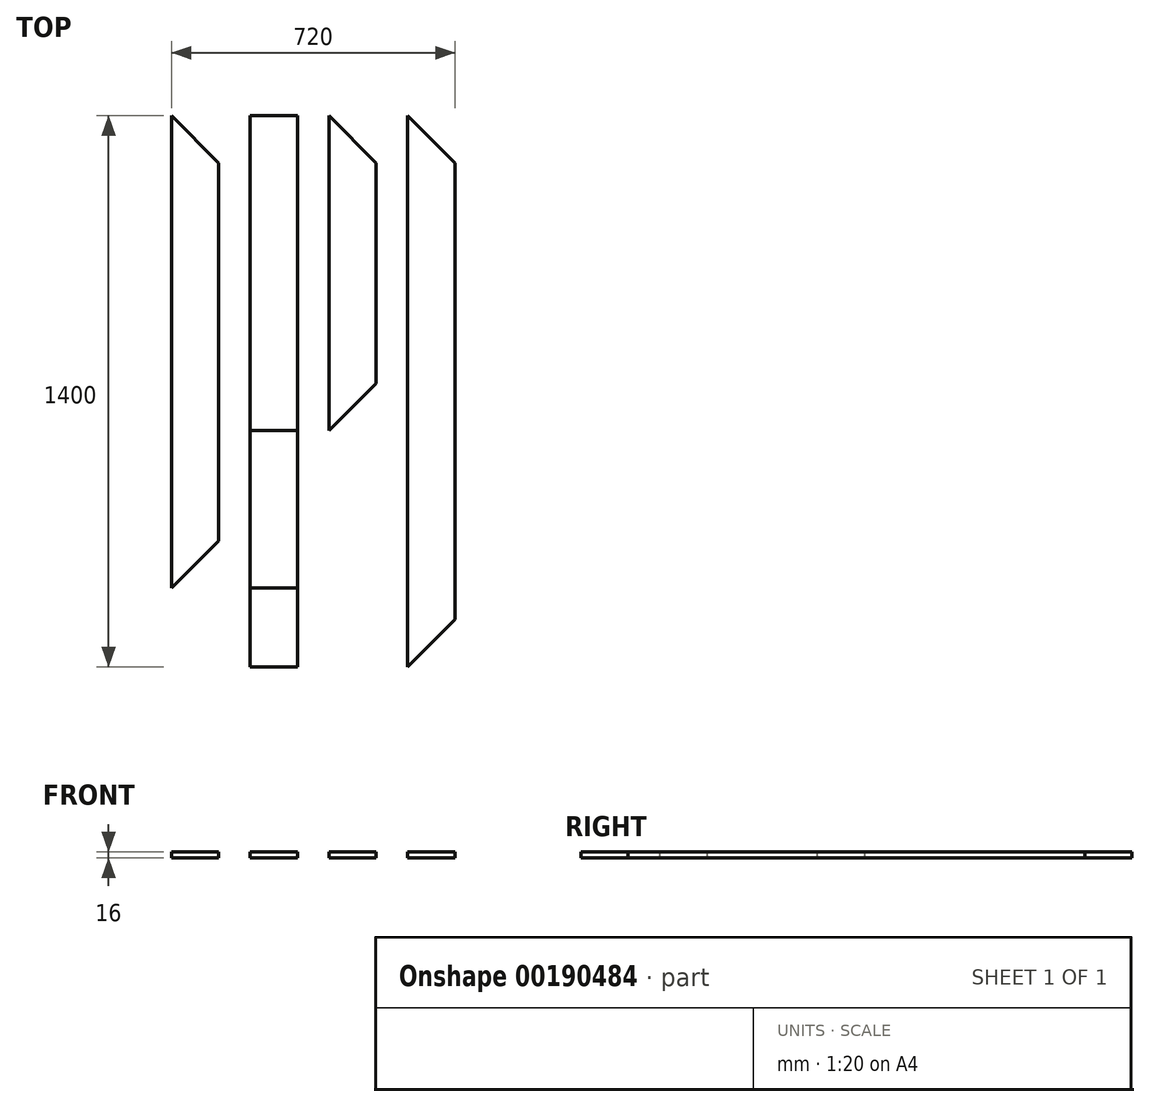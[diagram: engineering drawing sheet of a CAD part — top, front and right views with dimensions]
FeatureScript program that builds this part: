
annotation { "Feature Type Name" : "Feature", "Feature Type Description" : "" }
export const myFeature = defineFeature(function(context is Context, id is Id, definition is map)
    precondition{}
    {
        {
            var Q0;
            Q0=qCreatedBy(makeId("Front.planeOp"),FACE);
            var sketch = newSketch(context, id + "F0", { "sketchPlane" : qUnion([Q0])});
            skLineSegment(sketch, "E0.bottom", {"start": v(-60, 8) * mm, "end": v(60, 8) * mm});
            skLineSegment(sketch, "E0.top", {"start": v(-60, -8) * mm, "end": v(60, -8) * mm});
            skLineSegment(sketch, "E0.left", {"start": v(-60, 8) * mm, "end": v(-60, -8) * mm});
            skLineSegment(sketch, "E0.right", {"start": v(60, 8) * mm, "end": v(60, -8) * mm});
            skSolve(sketch);
        }
        {
            var Q0;
            Q0 = qSketchRegion(id + "F0", true);
            extrude(context, id + "F1", {"entities" : qUnion([Q0]), "depth" : 800 * mm});
        }
        {
            var Q0;
            Q0 = qSketchRegion(id + "F0", true);
            extrude(context, id + "F2", {"entities" : qUnion([Q0]), "depth" : 1200 * mm});
        }
        {
            var Q0;
            Q0=makeQuery(id+"F1.opExtrude","SWEPT_BODY",BODY,{"disambiguationData":[OSD([sQuery(id+"F0.wireOp",EDGE,"E0.bottom"),sQuery(id+"F0.wireOp",EDGE,"E0.top"),sQuery(id+"F0.wireOp",EDGE,"E0.left"),sQuery(id+"F0.wireOp",EDGE,"E0.right")])]});
            transform(context, id + "F3", {"entities" : qUnion([Q0]), "transformType" : TransformType.TRANSLATION_3D, "dx" : 200 * mm, "dy" : 0 * mm, "dz" : 0 * mm, "makeCopy" : true});
        }
        {
            var Q0;
            Q0=makeQuery(id+"F3.opPattern","COPY",EDGE,{"derivedFrom":makeQuery(id+"F1.opExtrude","CAP_EDGE",EDGE,{"disambiguationData":[OSD([sQuery(id+"F0.wireOp",EDGE,"E0.right")])],"isStart":false}),"instanceName":"1"});
            var Q1;
            Q1=makeQuery(id+"F3.opPattern","COPY",EDGE,{"derivedFrom":makeQuery(id+"F1.opExtrude","CAP_EDGE",EDGE,{"disambiguationData":[OSD([sQuery(id+"F0.wireOp",EDGE,"E0.right")])],"isStart":true}),"instanceName":"1"});
            chamfer(context, id + "F4", {"entities" : qUnion([Q0, Q1]), "width" : 120 * mm, "tangentPropagation" : true});
        }
        {
            var Q0;
            Q0=makeQuery(id+"F2.opExtrude","SWEPT_BODY",BODY,{"disambiguationData":[OSD([sQuery(id+"F0.wireOp",EDGE,"E0.bottom"),sQuery(id+"F0.wireOp",EDGE,"E0.top"),sQuery(id+"F0.wireOp",EDGE,"E0.left"),sQuery(id+"F0.wireOp",EDGE,"E0.right")])]});
            transform(context, id + "F5", {"entities" : qUnion([Q0]), "transformType" : TransformType.TRANSLATION_3D, "dx" : -200 * mm, "dy" : 0 * mm, "dz" : 0 * mm, "makeCopy" : true});
        }
        {
            var Q0;
            Q0=makeQuery(id+"F5.opPattern","COPY",EDGE,{"derivedFrom":makeQuery(id+"F2.opExtrude","CAP_EDGE",EDGE,{"disambiguationData":[OSD([sQuery(id+"F0.wireOp",EDGE,"E0.right")])],"isStart":false}),"instanceName":"1"});
            var Q1;
            Q1=makeQuery(id+"F5.opPattern","COPY",EDGE,{"derivedFrom":makeQuery(id+"F2.opExtrude","CAP_EDGE",EDGE,{"disambiguationData":[OSD([sQuery(id+"F0.wireOp",EDGE,"E0.right")])],"isStart":true}),"instanceName":"1"});
            chamfer(context, id + "F6", {"entities" : qUnion([Q0, Q1]), "width" : 120 * mm, "tangentPropagation" : true});
        }
        {
            var Q0;
            Q0 = qSketchRegion(id + "F0", true);
            extrude(context, id + "F7", {"entities" : qUnion([Q0]), "depth" : 1400 * mm});
        }
        {
            var Q0;
            Q0=makeQuery(id+"F7.opExtrude","SWEPT_BODY",BODY,{"disambiguationData":[OSD([sQuery(id+"F0.wireOp",EDGE,"E0.bottom"),sQuery(id+"F0.wireOp",EDGE,"E0.top"),sQuery(id+"F0.wireOp",EDGE,"E0.left"),sQuery(id+"F0.wireOp",EDGE,"E0.right")])]});
            transform(context, id + "F8", {"entities" : qUnion([Q0]), "transformType" : TransformType.TRANSLATION_3D, "dx" : 400 * mm, "dy" : 0 * mm, "dz" : 0 * mm, "makeCopy" : true});
        }
        {
            var Q0;
            Q0=makeQuery(id+"F8.opPattern","COPY",EDGE,{"derivedFrom":makeQuery(id+"F7.opExtrude","CAP_EDGE",EDGE,{"disambiguationData":[OSD([sQuery(id+"F0.wireOp",EDGE,"E0.right")])],"isStart":false}),"instanceName":"1"});
            var Q1;
            Q1=makeQuery(id+"F8.opPattern","COPY",EDGE,{"derivedFrom":makeQuery(id+"F7.opExtrude","CAP_EDGE",EDGE,{"disambiguationData":[OSD([sQuery(id+"F0.wireOp",EDGE,"E0.right")])],"isStart":true}),"instanceName":"1"});
            chamfer(context, id + "F9", {"entities" : qUnion([Q0, Q1]), "width" : 120 * mm, "tangentPropagation" : true});
        }
    });
